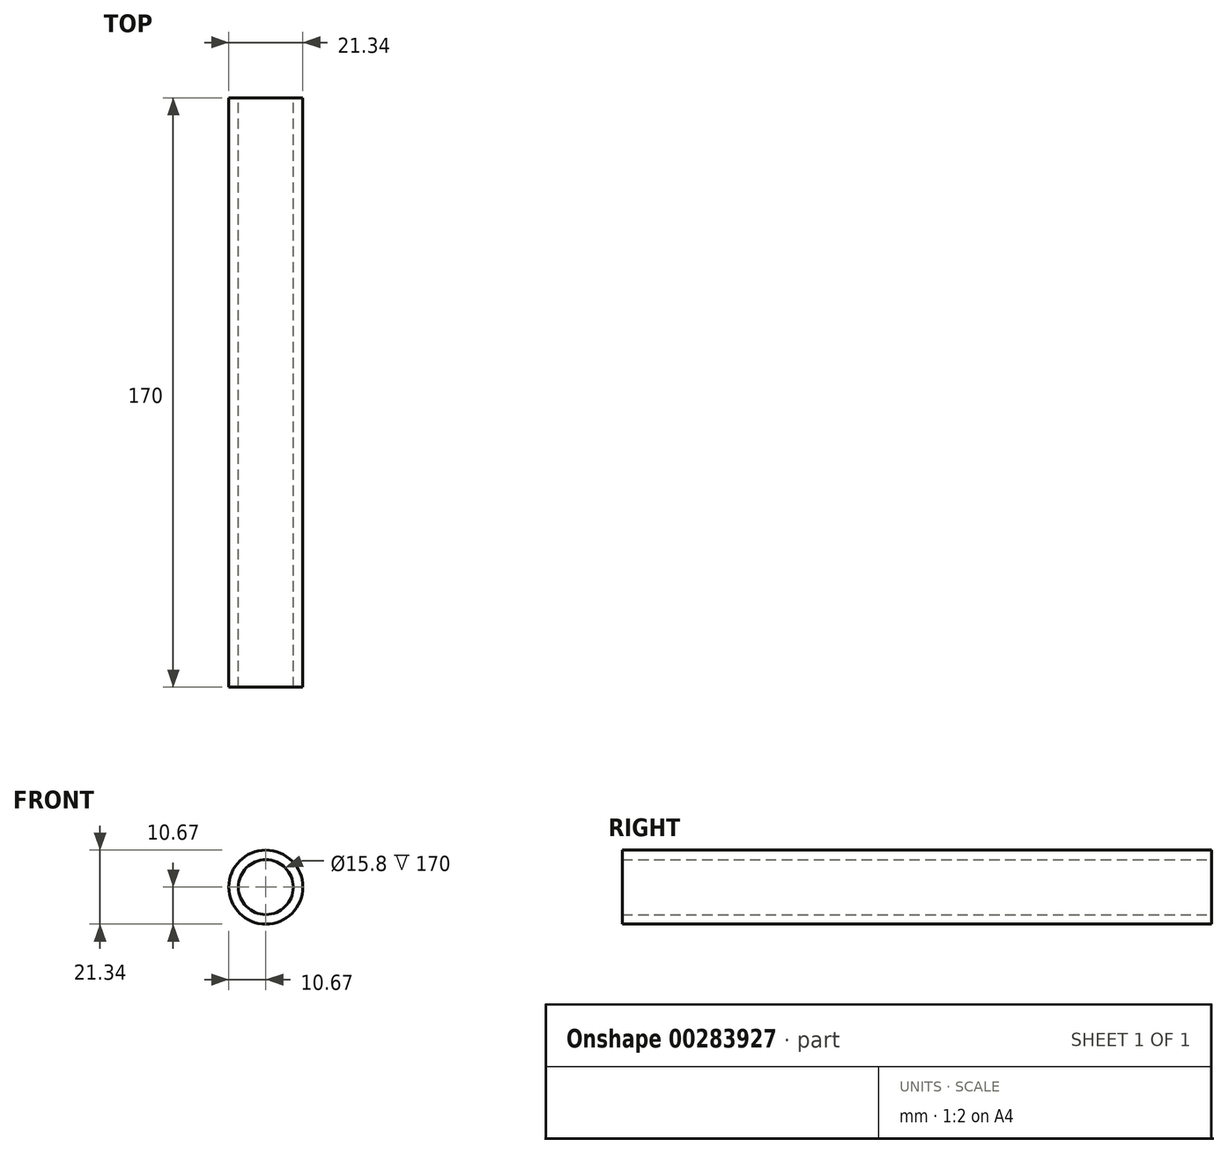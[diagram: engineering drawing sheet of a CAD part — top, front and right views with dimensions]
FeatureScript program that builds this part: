
annotation { "Feature Type Name" : "Feature", "Feature Type Description" : "" }
export const myFeature = defineFeature(function(context is Context, id is Id, definition is map)
    precondition{}
    {
        {
            var Q0;
            Q0=qCreatedBy(makeId("Front.planeOp"),FACE);
            var sketch = newSketch(context, id + "F0", { "sketchPlane" : qUnion([Q0])});
            skCircle(sketch, "E0", {"center": v(0, 0) * mm, "radius": 7.9 * mm});
            skCircle(sketch, "E1", {"center": v(0, 0) * mm, "radius": 10.67 * mm});
            skSolve(sketch);
        }
        {
            var Q0;
            Q0=qSketchRegion(id+"F0",true);
            extrude(context, id + "F1", {"entities" : qUnion([Q0]), "endBound" : BoundingType.SYMMETRIC, "depth" : 170 * mm});
        }
    });
